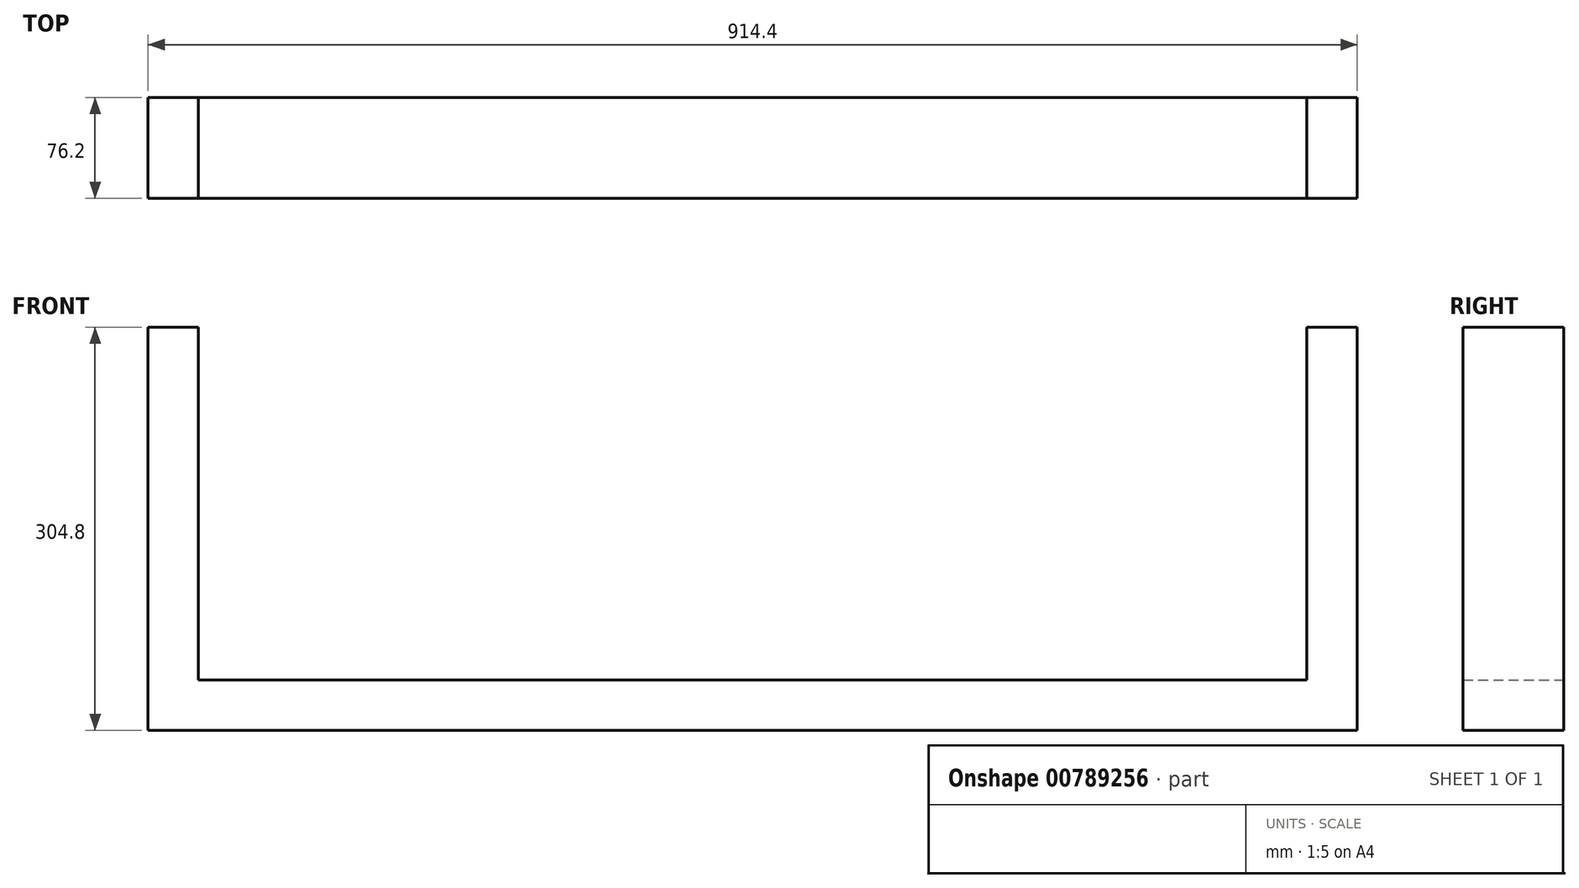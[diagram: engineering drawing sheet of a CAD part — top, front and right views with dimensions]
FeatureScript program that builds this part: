
annotation { "Feature Type Name" : "Feature", "Feature Type Description" : "" }
export const myFeature = defineFeature(function(context is Context, id is Id, definition is map)
    precondition{}
    {
        {
            var Q0;
            Q0=qCreatedBy(makeId("Front.planeOp"),FACE);
            var sketch = newSketch(context, id + "F0", { "sketchPlane" : qUnion([Q0])});
            skLineSegment(sketch, "E0", {"start": v(0, 0) * mm, "end": v(914.4, 0) * mm});
            skLineSegment(sketch, "E1", {"start": v(914.4, 0) * mm, "end": v(914.4, 304.8) * mm});
            skLineSegment(sketch, "E2", {"start": v(914.4, 304.8) * mm, "end": v(876.3, 304.8) * mm});
            skLineSegment(sketch, "E3", {"start": v(876.3, 304.8) * mm, "end": v(876.3, 38.1) * mm});
            skLineSegment(sketch, "E4", {"start": v(876.3, 38.1) * mm, "end": v(38.1, 38.1) * mm});
            skLineSegment(sketch, "E5", {"start": v(38.1, 38.1) * mm, "end": v(38.1, 304.8) * mm});
            skLineSegment(sketch, "E6", {"start": v(38.1, 304.8) * mm, "end": v(0, 304.8) * mm});
            skLineSegment(sketch, "E7", {"start": v(0, 304.8) * mm, "end": v(0, 0) * mm});
            skSolve(sketch);
        }
        {
            var Q0;
            Q0 = qSketchRegion(id + "F0", true);
            extrude(context, id + "F1", {"entities" : qUnion([Q0]), "endBound" : BoundingType.SYMMETRIC, "depth" : 76.2 * mm, "offsetDistance" : 25.4 * mm});
        }
    });
